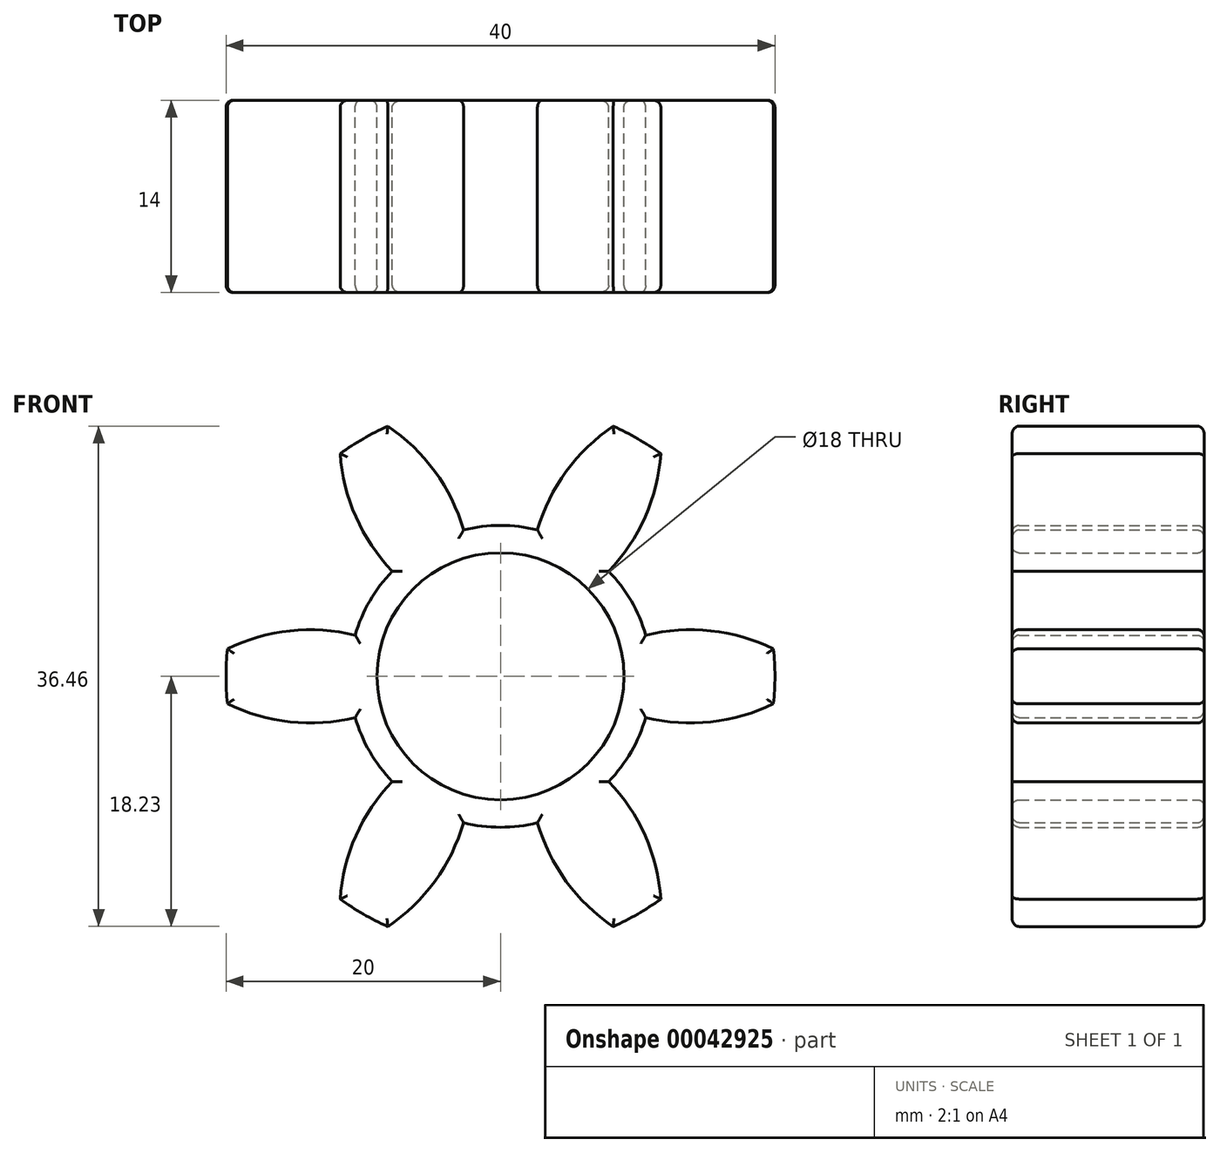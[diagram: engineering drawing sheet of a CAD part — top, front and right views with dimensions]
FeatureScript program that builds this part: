
annotation { "Feature Type Name" : "Feature", "Feature Type Description" : "" }
export const myFeature = defineFeature(function(context is Context, id is Id, definition is map)
    precondition{}
    {
        {
            var Q0;
            Q0=qCreatedBy(makeId("Front.planeOp"),FACE);
            var sketch = newSketch(context, id + "F0", { "sketchPlane" : qUnion([Q0])});
            skArc(sketch, "E0", {"start": v(-8.22, 18.23) * mm, "mid": v(-10, 17.32) * mm, "end": v(-11.68, 16.23) * mm});
            skCircle(sketch, "E1", {"center": v(0, 0) * mm, "radius": 9 * mm});
            skArc(sketch, "E2", {"start": v(-10.58, -3) * mm, "mid": v(-9.53, -5.5) * mm, "end": v(-7.89, -7.67) * mm});
            skArc(sketch, "E3", {"start": v(19.9, 2) * mm, "mid": v(15.33, 3.32) * mm, "end": v(10.58, 3) * mm});
            skArc(sketch, "E4.MirrorCS", {"start": v(19.9, -2) * mm, "mid": v(15.33, -3.32) * mm, "end": v(10.58, -3) * mm});
            skArc(sketch, "E5.1.0", {"start": v(8.22, 18.23) * mm, "mid": v(4.79, 14.94) * mm, "end": v(2.7, 10.67) * mm});
            skArc(sketch, "E5.1.1", {"start": v(11.68, 16.23) * mm, "mid": v(10.54, 11.62) * mm, "end": v(7.89, 7.67) * mm});
            skArc(sketch, "E5.2.0", {"start": v(-11.68, 16.23) * mm, "mid": v(-10.54, 11.62) * mm, "end": v(-7.89, 7.67) * mm});
            skArc(sketch, "E5.2.1", {"start": v(-8.22, 18.23) * mm, "mid": v(-4.79, 14.94) * mm, "end": v(-2.7, 10.67) * mm});
            skArc(sketch, "E5.3.0", {"start": v(-19.9, -2) * mm, "mid": v(-15.33, -3.32) * mm, "end": v(-10.58, -3) * mm});
            skArc(sketch, "E5.3.1", {"start": v(-19.9, 2) * mm, "mid": v(-15.33, 3.32) * mm, "end": v(-10.58, 3) * mm});
            skArc(sketch, "E5.4.0", {"start": v(-8.22, -18.23) * mm, "mid": v(-4.79, -14.94) * mm, "end": v(-2.7, -10.67) * mm});
            skArc(sketch, "E5.4.1", {"start": v(-11.68, -16.23) * mm, "mid": v(-10.54, -11.62) * mm, "end": v(-7.89, -7.67) * mm});
            skArc(sketch, "E5.5.0", {"start": v(11.68, -16.23) * mm, "mid": v(10.54, -11.62) * mm, "end": v(7.89, -7.67) * mm});
            skArc(sketch, "E5.5.1", {"start": v(8.22, -18.23) * mm, "mid": v(4.79, -14.94) * mm, "end": v(2.7, -10.67) * mm});
            skArc(sketch, "E6.trimOffspring", {"start": v(-19.9, 2) * mm, "mid": v(-20, 0) * mm, "end": v(-19.9, -2) * mm});
            skArc(sketch, "E7.trimOffspring", {"start": v(-7.89, 7.67) * mm, "mid": v(-9.53, 5.5) * mm, "end": v(-10.58, 3) * mm});
            skArc(sketch, "E8.trimOffspring", {"start": v(2.7, 10.67) * mm, "mid": v(0, 11) * mm, "end": v(-2.7, 10.67) * mm});
            skArc(sketch, "E9.trimOffspring", {"start": v(11.68, 16.23) * mm, "mid": v(10, 17.32) * mm, "end": v(8.22, 18.23) * mm});
            skArc(sketch, "E10.trimOffspring", {"start": v(19.9, -2) * mm, "mid": v(20, 0) * mm, "end": v(19.9, 2) * mm});
            skArc(sketch, "E11.trimOffspring", {"start": v(10.58, 3) * mm, "mid": v(9.53, 5.5) * mm, "end": v(7.89, 7.67) * mm});
            skArc(sketch, "E12.trimOffspring", {"start": v(8.22, -18.23) * mm, "mid": v(10, -17.32) * mm, "end": v(11.68, -16.23) * mm});
            skArc(sketch, "E13.trimOffspring", {"start": v(7.89, -7.67) * mm, "mid": v(9.53, -5.5) * mm, "end": v(10.58, -3) * mm});
            skArc(sketch, "E14.trimOffspring", {"start": v(-2.7, -10.67) * mm, "mid": v(0, -11) * mm, "end": v(2.7, -10.67) * mm});
            skArc(sketch, "E15.trimOffspring", {"start": v(-11.68, -16.23) * mm, "mid": v(-10, -17.32) * mm, "end": v(-8.22, -18.23) * mm});
            skSolve(sketch);
        }
        {
            var Q0;
            Q0=makeQuery(id+"F0.imprint","IMPRINT",FACE,{"disambiguationData":[TD([[makeQuery(id+"F0.imprint","IMPRINT",EDGE,{"derivedFrom":sQuery(id+"F0.wireOp",EDGE,"E0")}),1.0]])]});
            extrude(context, id + "F1", {"entities" : qUnion([Q0]), "depth" : 14 * mm});
        }
        {
            var Q0;
            Q0=makeQuery(id+"F1.opExtrude","CAP_FACE",FACE,{"disambiguationData":[OSD([sQuery(id+"F0.wireOp",EDGE,"E0"),sQuery(id+"F0.wireOp",EDGE,"E1"),sQuery(id+"F0.wireOp",EDGE,"E2"),sQuery(id+"F0.wireOp",EDGE,"E3"),sQuery(id+"F0.wireOp",EDGE,"E4.MirrorCS"),sQuery(id+"F0.wireOp",EDGE,"E5.1.0"),sQuery(id+"F0.wireOp",EDGE,"E5.1.1"),sQuery(id+"F0.wireOp",EDGE,"E5.2.0"),sQuery(id+"F0.wireOp",EDGE,"E5.2.1"),sQuery(id+"F0.wireOp",EDGE,"E5.3.0"),sQuery(id+"F0.wireOp",EDGE,"E5.3.1"),sQuery(id+"F0.wireOp",EDGE,"E5.4.0"),sQuery(id+"F0.wireOp",EDGE,"E5.4.1"),sQuery(id+"F0.wireOp",EDGE,"E5.5.0"),sQuery(id+"F0.wireOp",EDGE,"E5.5.1"),sQuery(id+"F0.wireOp",EDGE,"E6.trimOffspring"),sQuery(id+"F0.wireOp",EDGE,"E7.trimOffspring"),sQuery(id+"F0.wireOp",EDGE,"E8.trimOffspring"),sQuery(id+"F0.wireOp",EDGE,"E9.trimOffspring"),sQuery(id+"F0.wireOp",EDGE,"E10.trimOffspring"),sQuery(id+"F0.wireOp",EDGE,"E11.trimOffspring"),sQuery(id+"F0.wireOp",EDGE,"E12.trimOffspring"),sQuery(id+"F0.wireOp",EDGE,"E13.trimOffspring"),sQuery(id+"F0.wireOp",EDGE,"E14.trimOffspring"),sQuery(id+"F0.wireOp",EDGE,"E15.trimOffspring")])],"isStart":false});
            var Q1;
            Q1=makeQuery(id+"F1.opExtrude","CAP_FACE",FACE,{"disambiguationData":[OSD([sQuery(id+"F0.wireOp",EDGE,"E0"),sQuery(id+"F0.wireOp",EDGE,"E1"),sQuery(id+"F0.wireOp",EDGE,"E2"),sQuery(id+"F0.wireOp",EDGE,"E3"),sQuery(id+"F0.wireOp",EDGE,"E4.MirrorCS"),sQuery(id+"F0.wireOp",EDGE,"E5.1.0"),sQuery(id+"F0.wireOp",EDGE,"E5.1.1"),sQuery(id+"F0.wireOp",EDGE,"E5.2.0"),sQuery(id+"F0.wireOp",EDGE,"E5.2.1"),sQuery(id+"F0.wireOp",EDGE,"E5.3.0"),sQuery(id+"F0.wireOp",EDGE,"E5.3.1"),sQuery(id+"F0.wireOp",EDGE,"E5.4.0"),sQuery(id+"F0.wireOp",EDGE,"E5.4.1"),sQuery(id+"F0.wireOp",EDGE,"E5.5.0"),sQuery(id+"F0.wireOp",EDGE,"E5.5.1"),sQuery(id+"F0.wireOp",EDGE,"E6.trimOffspring"),sQuery(id+"F0.wireOp",EDGE,"E7.trimOffspring"),sQuery(id+"F0.wireOp",EDGE,"E8.trimOffspring"),sQuery(id+"F0.wireOp",EDGE,"E9.trimOffspring"),sQuery(id+"F0.wireOp",EDGE,"E10.trimOffspring"),sQuery(id+"F0.wireOp",EDGE,"E11.trimOffspring"),sQuery(id+"F0.wireOp",EDGE,"E12.trimOffspring"),sQuery(id+"F0.wireOp",EDGE,"E13.trimOffspring"),sQuery(id+"F0.wireOp",EDGE,"E14.trimOffspring"),sQuery(id+"F0.wireOp",EDGE,"E15.trimOffspring")])],"isStart":true});
            fillet(context, id + "F2", {"entities" : qUnion([Q0, Q1]), "radius" : .5 * mm, "tangentPropagation" : true, "allowEdgeOverflow" : false});
        }
    });
